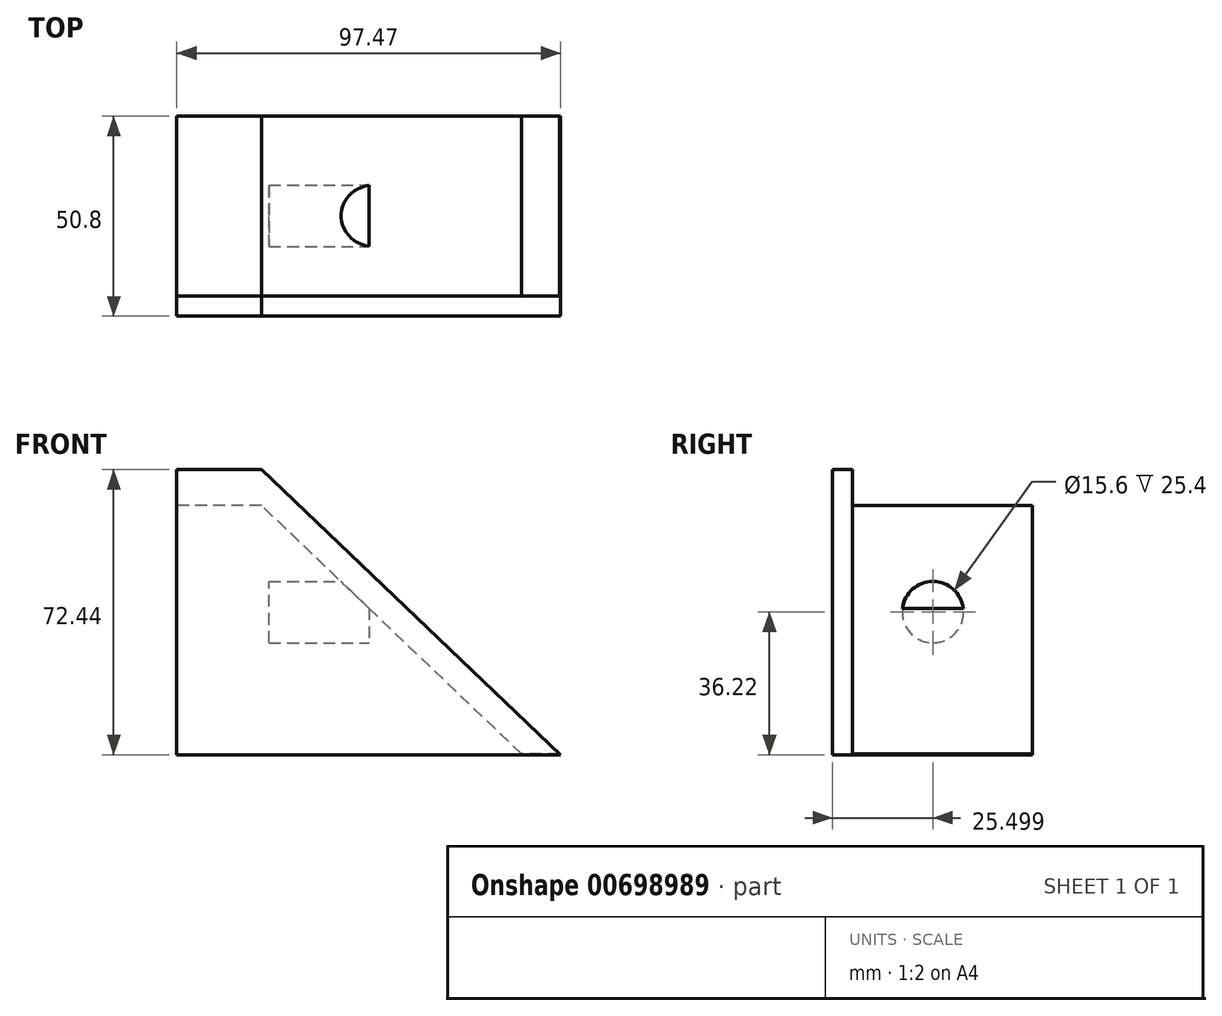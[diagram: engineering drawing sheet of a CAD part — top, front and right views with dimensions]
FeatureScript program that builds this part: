
annotation { "Feature Type Name" : "Feature", "Feature Type Description" : "" }
export const myFeature = defineFeature(function(context is Context, id is Id, definition is map)
    precondition{}
    {
        {
            var Q0;
            Q0=qCreatedBy(makeId("Front.planeOp"),FACE);
            var sketch = newSketch(context, id + "F0", { "sketchPlane" : qUnion([Q0])});
            skLineSegment(sketch, "E0", {"start": v(-48.83, 36.22) * mm, "end": v(-48.83, -36.22) * mm});
            skLineSegment(sketch, "E1", {"start": v(-48.83, -36.22) * mm, "end": v(48.64, -36.22) * mm});
            skLineSegment(sketch, "E2", {"start": v(-48.83, 36.22) * mm, "end": v(-27.35, 36.22) * mm});
            skLineSegment(sketch, "E3", {"start": v(-27.35, 36.22) * mm, "end": v(48.64, -36.22) * mm});
            skSolve(sketch);
        }
        {
            var Q0;
            Q0 = qSketchRegion(id + "F0", true);
            extrude(context, id + "F1", {"entities" : qUnion([Q0]), "depth" : 50.8 * mm, "offsetDistance" : 25.4 * mm});
        }
        {
            var Q0;
            Q0=qCreatedBy(makeId("Front.planeOp"),FACE);
            var sketch = newSketch(context, id + "F2", { "sketchPlane" : qUnion([Q0])});
            skLineSegment(sketch, "E4", {"start": v(-48.83, 36.6) * mm, "end": v(-27.35, 36.6) * mm});
            skLineSegment(sketch, "E5", {"start": v(-27.35, 36.6) * mm, "end": v(48.64, -36.04) * mm});
            skLineSegment(sketch, "E6", {"start": v(48.64, -36.04) * mm, "end": v(38.74, -36.04) * mm});
            skLineSegment(sketch, "E7", {"start": v(38.74, -36.04) * mm, "end": v(-27.35, 27.14) * mm});
            skLineSegment(sketch, "E8", {"start": v(-27.35, 27.14) * mm, "end": v(-48.83, 27.14) * mm});
            skLineSegment(sketch, "E9", {"start": v(-48.83, 27.14) * mm, "end": v(-48.83, 36.6) * mm});
            skSolve(sketch);
        }
        {
            var Q0;
            Q0 = qSketchRegion(id + "F2", true);
            extrude(context, id + "F3", {"entities" : qUnion([Q0]), "operationType" : NewBodyOperationType.REMOVE, "depth" : 45.72 * mm, "offsetDistance" : 25.4 * mm});
        }
        {
            var Q0;
            Q0=qCreatedBy(makeId("Right.planeOp"),FACE);
            var sketch = newSketch(context, id + "F4", { "sketchPlane" : qUnion([Q0])});
            skCircle(sketch, "E10", {"center": v(-25.3, 0) * mm, "radius": 7.8 * mm});
            skSolve(sketch);
        }
        {
            var Q0;
            Q0 = qSketchRegion(id + "F4", true);
            extrude(context, id + "F5", {"entities" : qUnion([Q0]), "operationType" : NewBodyOperationType.REMOVE, "oppositeDirection" : true, "depth" : 25.4 * mm, "offsetDistance" : 25.4 * mm});
        }
    });
